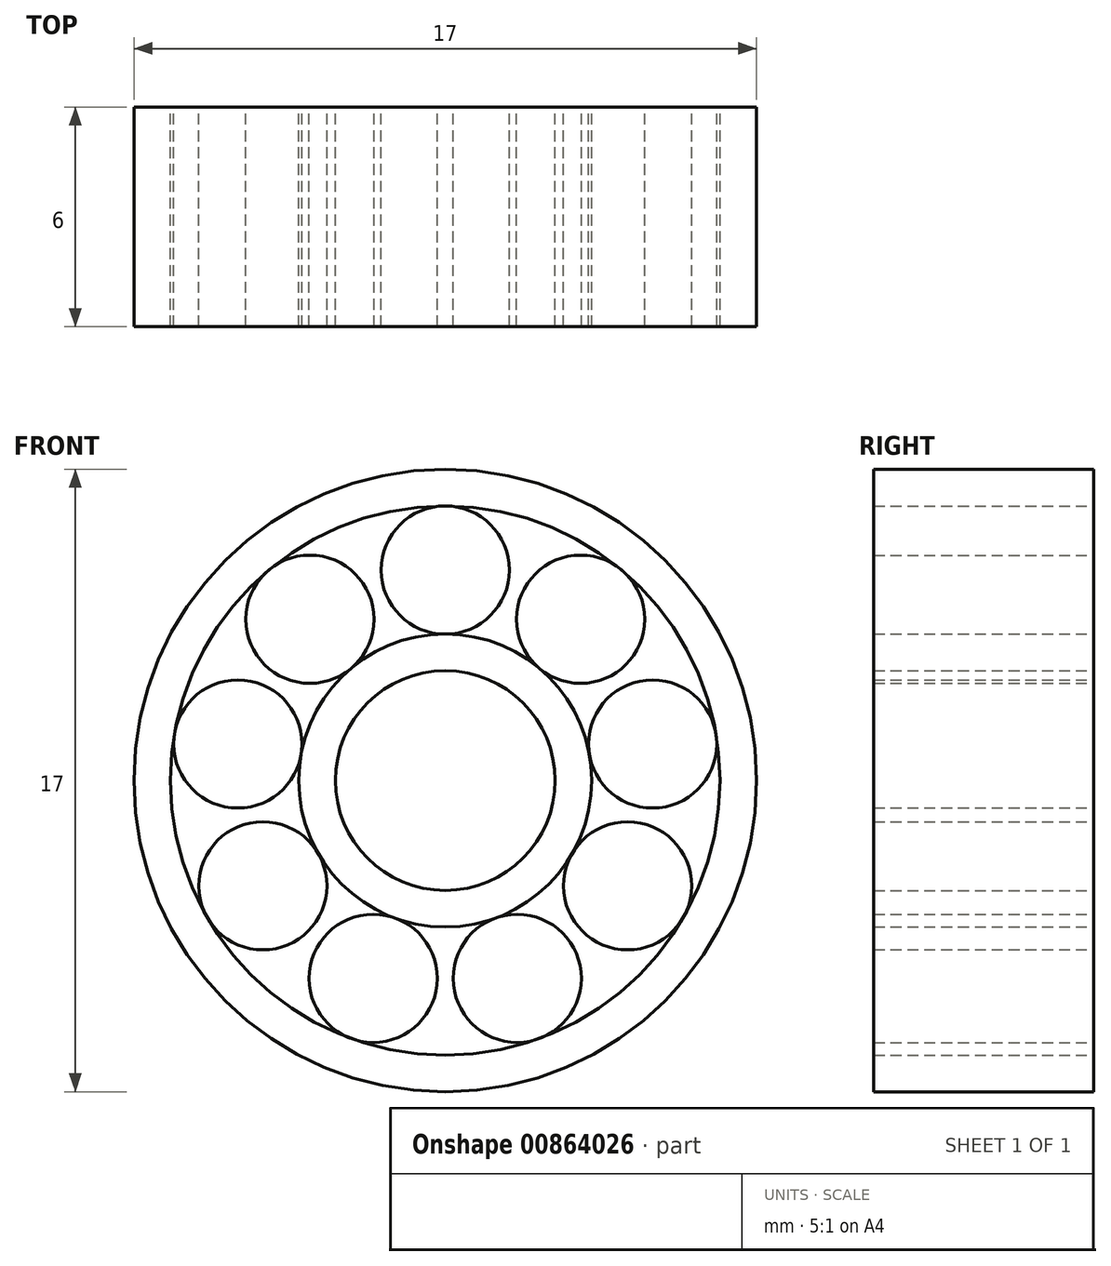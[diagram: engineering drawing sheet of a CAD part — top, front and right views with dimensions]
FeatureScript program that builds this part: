
annotation { "Feature Type Name" : "Feature", "Feature Type Description" : "" }
export const myFeature = defineFeature(function(context is Context, id is Id, definition is map)
    precondition{}
    {
        {
            var Q0;
            Q0=qCreatedBy(makeId("Front.planeOp"),FACE);
            var sketch = newSketch(context, id + "F0", { "sketchPlane" : qUnion([Q0])});
            skCircle(sketch, "E0", {"center": v(0, 0) * mm, "radius": 8.5 * mm});
            skCircle(sketch, "E1", {"center": v(0, 0) * mm, "radius": 7.5 * mm});
            skCircle(sketch, "E2", {"center": v(0, 0) * mm, "radius": 3 * mm});
            skCircle(sketch, "E3", {"center": v(0, 0) * mm, "radius": 4 * mm});
            skCircle(sketch, "E4", {"center": v(0, 5.75) * mm, "radius": 1.75 * mm});
            skCircle(sketch, "E5.1.0", {"center": v(-3.7, 4.4) * mm, "radius": 1.75 * mm});
            skCircle(sketch, "E5.2.0", {"center": v(-5.66, 1) * mm, "radius": 1.75 * mm});
            skCircle(sketch, "E5.3.0", {"center": v(-4.98, -2.87) * mm, "radius": 1.75 * mm});
            skCircle(sketch, "E5.4.0", {"center": v(-1.97, -5.4) * mm, "radius": 1.75 * mm});
            skCircle(sketch, "E5.5.0", {"center": v(1.97, -5.4) * mm, "radius": 1.75 * mm});
            skCircle(sketch, "E5.6.0", {"center": v(4.98, -2.88) * mm, "radius": 1.75 * mm});
            skCircle(sketch, "E5.7.0", {"center": v(5.66, 1) * mm, "radius": 1.75 * mm});
            skCircle(sketch, "E5.8.0", {"center": v(3.7, 4.4) * mm, "radius": 1.75 * mm});
            skSolve(sketch);
        }
        {
            var Q0;
            Q0=makeQuery(id+"F0.imprint","IMPRINT",FACE,{"disambiguationData":[TD([[makeQuery(id+"F0.imprint","IMPRINT",EDGE,{"derivedFrom":sQuery(id+"F0.wireOp",EDGE,"E0")}),1.0]])]});
            var Q1;
            {var subQ0=sQuery(id+"F0.wireOp",EDGE,"E5.1.0");var subQ1=makeQuery(id+"F0.imprint","INTERSECT",VERTEX,{"derivedFrom":[sQuery(id+"F0.wireOp",EDGE,"E1"),subQ0]});Q1=makeQuery(id+"F0.imprint","IMPRINT",FACE,{"disambiguationData":[TD([[makeQuery(id+"F0.imprint","IMPRINT",EDGE,{"disambiguationData":[TD([[subQ1,-1.0]])],"derivedFrom":subQ0}),1.0]])]});}
            var Q2;
            {var subQ0=sQuery(id+"F0.wireOp",EDGE,"E5.2.0");var subQ1=makeQuery(id+"F0.imprint","INTERSECT",VERTEX,{"derivedFrom":[sQuery(id+"F0.wireOp",EDGE,"E1"),subQ0]});Q2=makeQuery(id+"F0.imprint","IMPRINT",FACE,{"disambiguationData":[TD([[makeQuery(id+"F0.imprint","IMPRINT",EDGE,{"disambiguationData":[TD([[subQ1,-1.0]])],"derivedFrom":subQ0}),1.0]])]});}
            var Q3;
            {var subQ0=sQuery(id+"F0.wireOp",EDGE,"E5.3.0");var subQ1=makeQuery(id+"F0.imprint","INTERSECT",VERTEX,{"derivedFrom":[sQuery(id+"F0.wireOp",EDGE,"E1"),subQ0]});Q3=makeQuery(id+"F0.imprint","IMPRINT",FACE,{"disambiguationData":[TD([[makeQuery(id+"F0.imprint","IMPRINT",EDGE,{"disambiguationData":[TD([[subQ1,-1.0]])],"derivedFrom":subQ0}),1.0]])]});}
            var Q4;
            Q4=makeQuery(id+"F0.imprint","IMPRINT",FACE,{"disambiguationData":[TD([[makeQuery(id+"F0.imprint","IMPRINT",EDGE,{"derivedFrom":sQuery(id+"F0.wireOp",EDGE,"E2")}),-1.0]])]});
            var Q5;
            {var subQ0=sQuery(id+"F0.wireOp",EDGE,"E4");var subQ1=makeQuery(id+"F0.imprint","INTERSECT",VERTEX,{"derivedFrom":[sQuery(id+"F0.wireOp",EDGE,"E1"),subQ0]});Q5=makeQuery(id+"F0.imprint","IMPRINT",FACE,{"disambiguationData":[TD([[makeQuery(id+"F0.imprint","IMPRINT",EDGE,{"disambiguationData":[TD([[subQ1,-1.0]])],"derivedFrom":subQ0}),1.0]])]});}
            var Q6;
            {var subQ0=sQuery(id+"F0.wireOp",EDGE,"E5.8.0");var subQ1=makeQuery(id+"F0.imprint","INTERSECT",VERTEX,{"derivedFrom":[sQuery(id+"F0.wireOp",EDGE,"E1"),subQ0]});Q6=makeQuery(id+"F0.imprint","IMPRINT",FACE,{"disambiguationData":[TD([[makeQuery(id+"F0.imprint","IMPRINT",EDGE,{"disambiguationData":[TD([[subQ1,-1.0]])],"derivedFrom":subQ0}),1.0]])]});}
            var Q7;
            {var subQ0=sQuery(id+"F0.wireOp",EDGE,"E5.7.0");var subQ1=makeQuery(id+"F0.imprint","INTERSECT",VERTEX,{"derivedFrom":[sQuery(id+"F0.wireOp",EDGE,"E1"),subQ0]});Q7=makeQuery(id+"F0.imprint","IMPRINT",FACE,{"disambiguationData":[TD([[makeQuery(id+"F0.imprint","IMPRINT",EDGE,{"disambiguationData":[TD([[subQ1,-1.0]])],"derivedFrom":subQ0}),1.0]])]});}
            var Q8;
            {var subQ0=sQuery(id+"F0.wireOp",EDGE,"E5.6.0");var subQ1=makeQuery(id+"F0.imprint","INTERSECT",VERTEX,{"derivedFrom":[sQuery(id+"F0.wireOp",EDGE,"E1"),subQ0]});Q8=makeQuery(id+"F0.imprint","IMPRINT",FACE,{"disambiguationData":[TD([[makeQuery(id+"F0.imprint","IMPRINT",EDGE,{"disambiguationData":[TD([[subQ1,-1.0]])],"derivedFrom":subQ0}),1.0]])]});}
            var Q9;
            {var subQ0=sQuery(id+"F0.wireOp",EDGE,"E5.5.0");var subQ1=makeQuery(id+"F0.imprint","INTERSECT",VERTEX,{"derivedFrom":[sQuery(id+"F0.wireOp",EDGE,"E1"),subQ0]});Q9=makeQuery(id+"F0.imprint","IMPRINT",FACE,{"disambiguationData":[TD([[makeQuery(id+"F0.imprint","IMPRINT",EDGE,{"disambiguationData":[TD([[subQ1,-1.0]])],"derivedFrom":subQ0}),1.0]])]});}
            var Q10;
            {var subQ0=sQuery(id+"F0.wireOp",EDGE,"E5.4.0");var subQ1=makeQuery(id+"F0.imprint","INTERSECT",VERTEX,{"derivedFrom":[sQuery(id+"F0.wireOp",EDGE,"E1"),subQ0]});Q10=makeQuery(id+"F0.imprint","IMPRINT",FACE,{"disambiguationData":[TD([[makeQuery(id+"F0.imprint","IMPRINT",EDGE,{"disambiguationData":[TD([[subQ1,-1.0]])],"derivedFrom":subQ0}),1.0]])]});}
            extrude(context, id + "F1", {"entities" : qUnion([Q0, Q1, Q2, Q3, Q4, Q5, Q6, Q7, Q8, Q9, Q10]), "depth" : 6 * mm, "offsetDistance" : 25 * mm});
        }
    });
